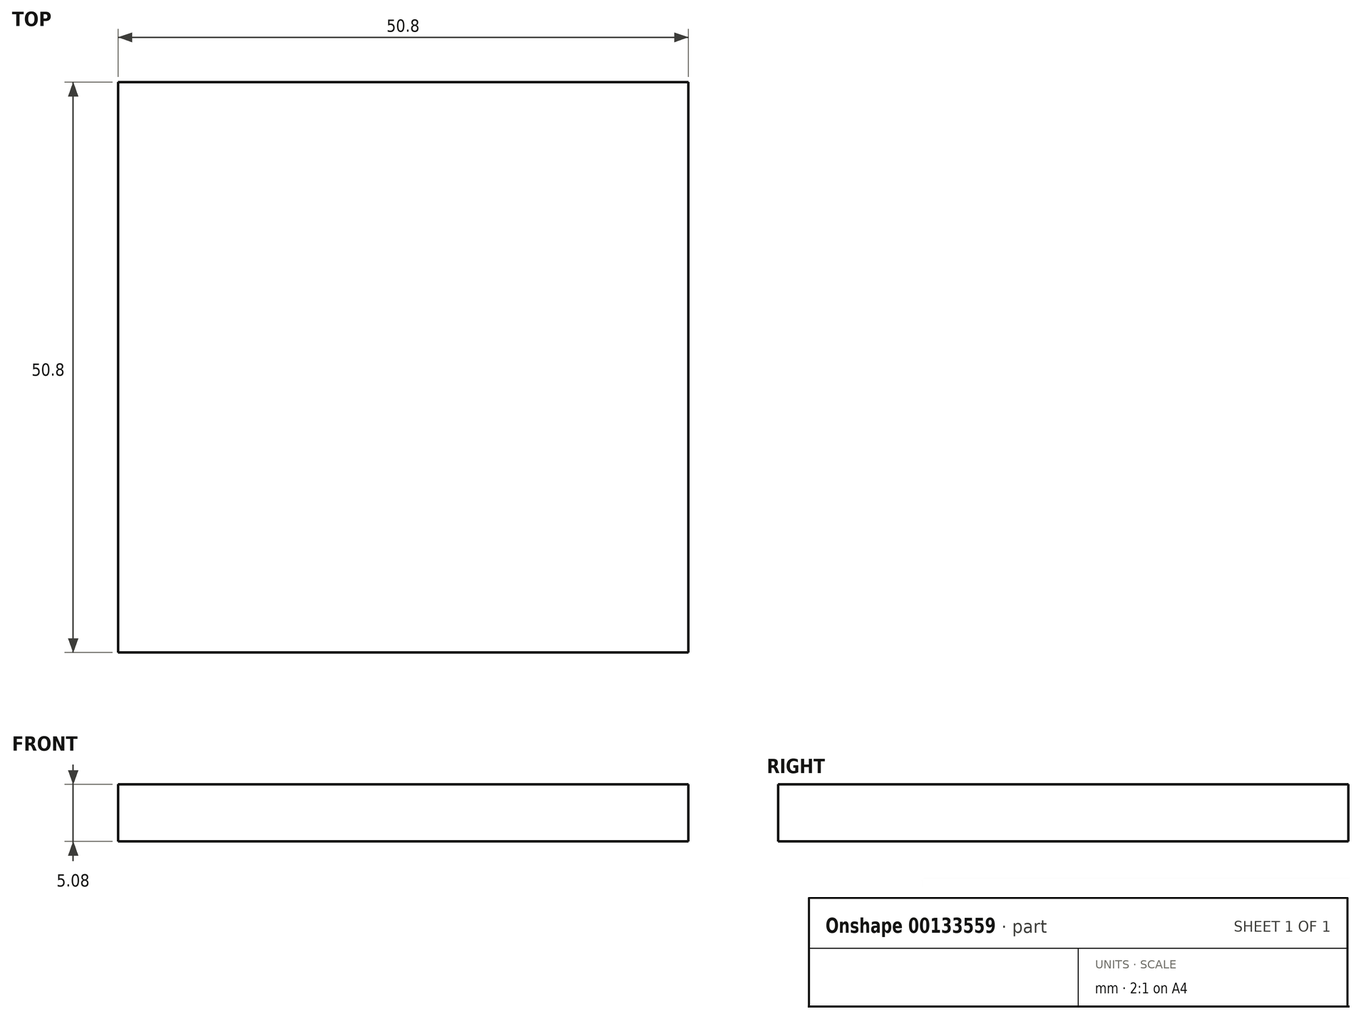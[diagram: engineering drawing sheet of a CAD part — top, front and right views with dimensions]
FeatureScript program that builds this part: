
annotation { "Feature Type Name" : "Feature", "Feature Type Description" : "" }
export const myFeature = defineFeature(function(context is Context, id is Id, definition is map)
    precondition{}
    {
        {
            var Q0;
            Q0=qCreatedBy(makeId("Top.planeOp"),FACE);
            var sketch = newSketch(context, id + "F0", { "sketchPlane" : qUnion([Q0])});
            skLineSegment(sketch, "E0.bottom", {"start": v(-23.92, 22) * mm, "end": v(26.88, 22) * mm});
            skLineSegment(sketch, "E0.top", {"start": v(-23.92, -28.8) * mm, "end": v(26.88, -28.8) * mm});
            skLineSegment(sketch, "E0.left", {"start": v(-23.92, 22) * mm, "end": v(-23.92, -28.8) * mm});
            skLineSegment(sketch, "E0.right", {"start": v(26.88, 22) * mm, "end": v(26.88, -28.8) * mm});
            skSolve(sketch);
        }
        {
            var Q0;
            Q0 = qSketchRegion(id + "F0", true);
            extrude(context, id + "F1", {"entities" : qUnion([Q0]), "depth" : 5.08 * mm});
        }
    });
